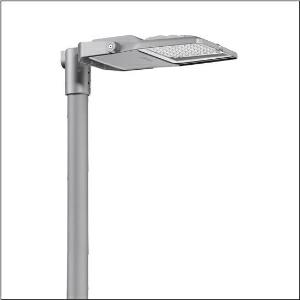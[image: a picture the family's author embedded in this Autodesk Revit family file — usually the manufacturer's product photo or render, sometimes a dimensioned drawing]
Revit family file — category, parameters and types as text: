
# Revit family: floodlight_fl_21_mini___pl61_5xa7776d2c3a_4c8f
name_source: partatom
category: Lighting Fixtures
units: mm (PartAtom-declared; Revit-internal decimal feet)

## family parameters
Cut with Voids When Loaded = No
Host = Face
Light Source = No
Part Type = Normal
Room Calculation Point = No
Round Connector Dimension = Use Diameter
Shared = No

## types (1)
- --- (1 x LED, 17510 lm, 142.9 W, 3000K)
    Apparent Load = 143 VA
    CIE Flux Codes = 33 65 98 100 100
    Color Rendering = 70
    Color Temperature = 3000K
    Default Elevation = 1800 mm
    Description = Floodlight FL 21 mini, floodlight, primary light control with lens, of PMMA, primary optical cover: protective disc, of toughened safety glass, transparent, light distribution: PL61, light emission: direct distribution, installation type: surface-mounted, LED, High Power LED, rated luminous flux: 17.510lm, luminous efficacy: 123lm/W, light colour: 730, colour temperature: 3000K, control: flexible luminous flux parameterisation, time-dependent luminous flux control, constant luminous flux control, overheat protection, presetting dimming logarithmic, with terminal, 6-pole, mains connection: 220..240V, AC, 50/60Hz, start of lifetime: 143W, end of service life: 151W, reduction: 63W, luminaire housing, of diecast aluminium, powder-coated, Siteco® metallic grey (DB 702S), corrosivity category C5 mid according to DIN EN ISO 12944, sealing non-destructively replaceable, please order mast flange separately, mast bracket, of steel, galvanised, powder-coated, Siteco® metallic grey (DB 702S), Smart Interface below and above, protection rating (complete): IP66, insulation class (complete): insulation class II (safety insulation), certification: CE, ENEC, VDE, protection symbol: D, impact resistance: IK08, permissible operating ambient temperature: -40..+40°C, permissible operating ambient temperature for outdoor applications: -40..+50°C, standard: DIN EN 12944, LABS conformity tested according to VDMA 24364:2018-05, packaging unit: 1 piece

Light Distribution: PL61
    Height = 70 mm
    Lamp = 1 x LED
    Lamp Light Flux = 17510 lm
    Lamp Power = 142.9 W
    Lamp count = 1
    Length = 485 mm
    Luminous efficacy = 123 lm/W
    Manufacturer = Siteco
    ModVariant = No
    Model = 5XA7776D2C3A
    Number of Poles = 1
    OnlyDefault = Yes
    Power Factor = 1
    Product Name = Floodlight FL 21 mini | PL61
    Product group = floodlight | pylon annexe
    ProductGroupID = 6200
    Protection Class = Protection class II
    Protection Degree = IP 66
    RLX_Detail_Level = 1
    RLX_Emergency_Light_Flux = 0 lm
    RLX_Emergency_Type = 0
    RLX_Emergency_Type_DB = No
    RlxData = <blob elided: 101285 chars, md5=cbb36df7>
    Socket = socket
    Standby Power = 0 W
    System Light Flux = 17510 lm
    System Power = 143 W
    Type Comments = factory setting: luminous flux: 100 % | dim-lin: 254 | 730 mA
    Type Image = l_1007125.jpg
    URL = http://relux.com
    VarID = @adj_122781
    Voltage = 0 V
    Weight = 0.00 kg
    Width = 337 mm

## geometry (parser evidence)
native form markers: Blend x4, Sweep x13
no freeform markers — native parametric forms only
